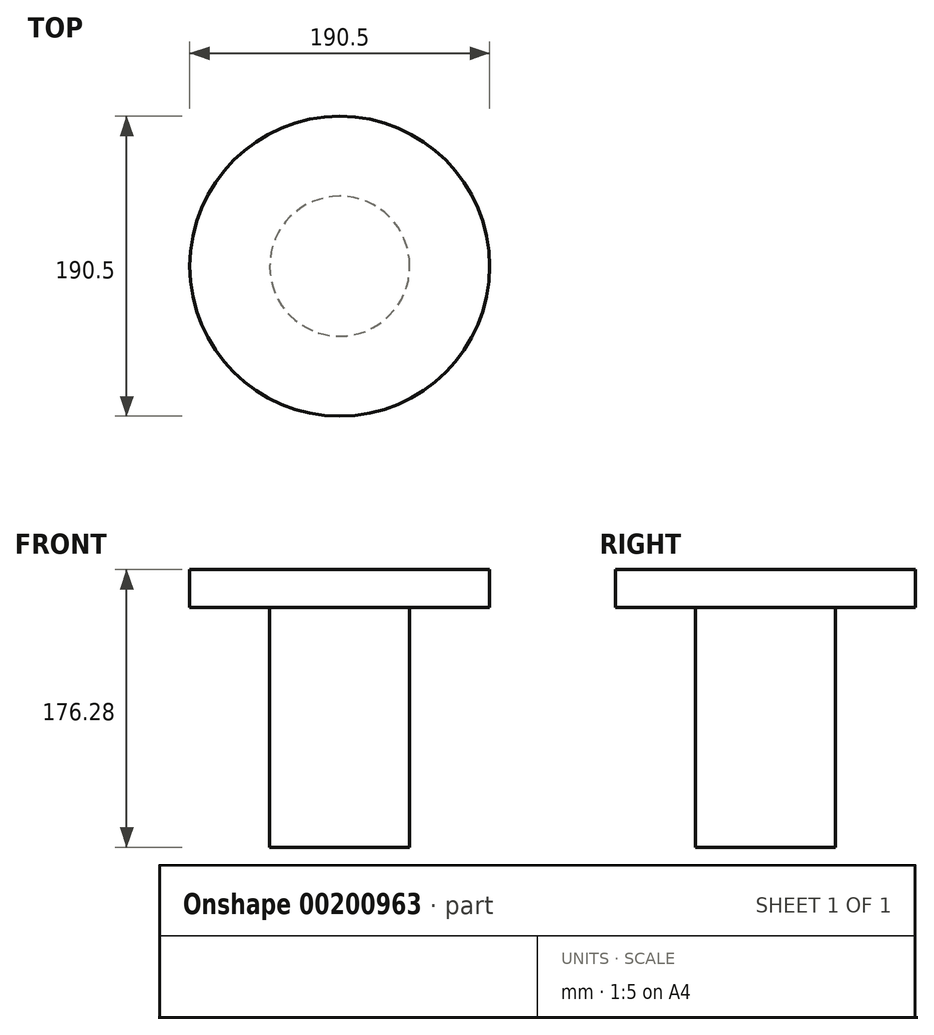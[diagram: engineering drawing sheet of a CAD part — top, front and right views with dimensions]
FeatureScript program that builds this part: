
annotation { "Feature Type Name" : "Feature", "Feature Type Description" : "" }
export const myFeature = defineFeature(function(context is Context, id is Id, definition is map)
    precondition{}
    {
        {
            var Q0;
            Q0=qCreatedBy(makeId("Front.planeOp"),FACE);
            var sketch = newSketch(context, id + "F0", { "sketchPlane" : qUnion([Q0])});
            skLineSegment(sketch, "E0", {"start": v(0, 0) * mm, "end": v(0, 335.65) * mm});
            skLineSegment(sketch, "E1", {"start": v(0, 0) * mm, "end": v(0, 176.28) * mm});
            skLineSegment(sketch, "E2", {"start": v(0, 176.28) * mm, "end": v(95.25, 176.28) * mm});
            skLineSegment(sketch, "E3", {"start": v(95.25, 176.28) * mm, "end": v(95.25, 152.4) * mm});
            skLineSegment(sketch, "E4", {"start": v(95.25, 152.4) * mm, "end": v(44.45, 152.4) * mm});
            skLineSegment(sketch, "E5", {"start": v(44.45, 152.4) * mm, "end": v(44.45, 0) * mm});
            skLineSegment(sketch, "E6", {"start": v(44.45, 0) * mm, "end": v(0, 0) * mm});
            skSolve(sketch);
        }
        {
            var Q0;
            {var subQ0=sQuery(id+"F0.wireOp",EDGE,"E2");Q0=makeQuery(id+"F0.imprint","IMPRINT",FACE,{"disambiguationData":[TD([[makeQuery(id+"F0.imprint","IMPRINT",EDGE,{"derivedFrom":subQ0}),-1.0]])]});}
            var Q1;
            Q1=sQuery(id+"F0.wireOp",EDGE,"E0");
            revolve(context, id + "F1", {"surfaceOperationType" : NewSurfaceOperationType.NEW, "entities" : qUnion([Q0]), "axis" : qUnion([Q1]), "revolveType" : RevolveType.FULL});
        }
    });
